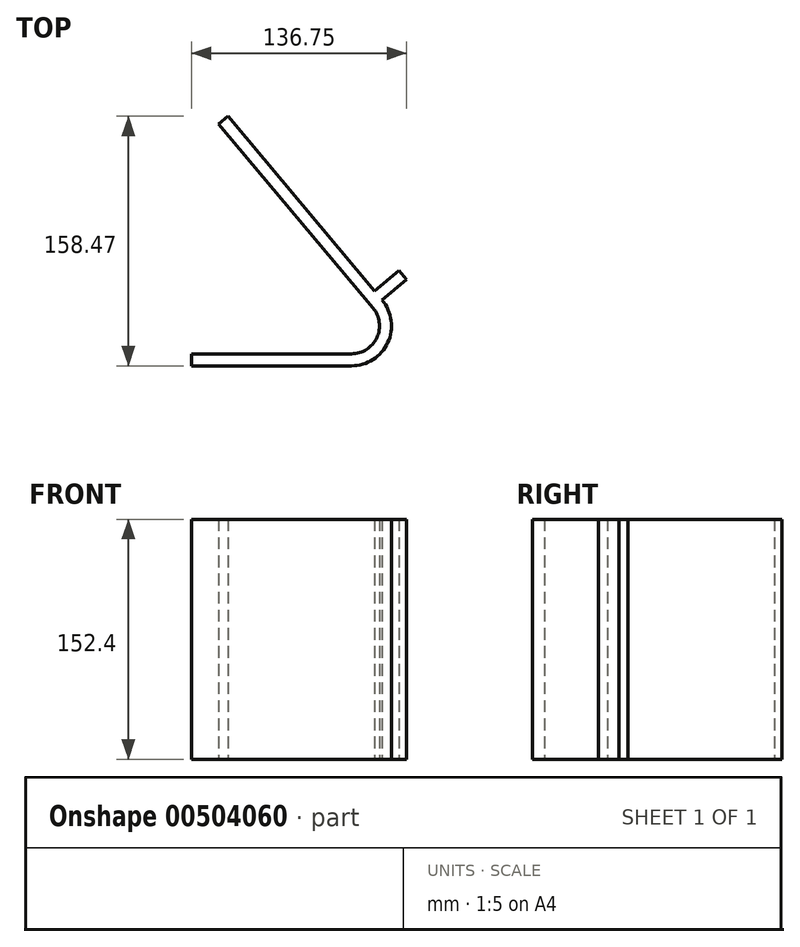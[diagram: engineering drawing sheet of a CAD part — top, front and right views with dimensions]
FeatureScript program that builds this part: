
annotation { "Feature Type Name" : "Feature", "Feature Type Description" : "" }
export const myFeature = defineFeature(function(context is Context, id is Id, definition is map)
    precondition{}
    {
        {
            var Q0;
            Q0=qCreatedBy(makeId("Top.planeOp"),FACE);
            var sketch = newSketch(context, id + "F0", { "sketchPlane" : qUnion([Q0])});
            skLineSegment(sketch, "E0", {"start": v(-114.2, -40.5) * mm, "end": v(-12.6, -40.5) * mm});
            skLineSegment(sketch, "E1", {"start": v(1.96, 7.06) * mm, "end": v(-91.1, 117.97) * mm});
            skPoint(sketch, "E2.visualSharp", {"position": v(41.87, -40.5) * mm});
            skArc(sketch, "E2.filletArc", {"start": v(-12.6, -40.5) * mm, "mid": v(10.42, -25.84) * mm, "end": v(6.86, 1.23) * mm});
            skLineSegment(sketch, "E3", {"start": v(-91.1, 117.97) * mm, "end": v(-96.94, 113.07) * mm});
            skLineSegment(sketch, "E4", {"start": v(-96.94, 113.07) * mm, "end": v(1.02, -3.67) * mm});
            skLineSegment(sketch, "E5", {"start": v(-12.6, -32.88) * mm, "end": v(-114.32, -32.88) * mm});
            skLineSegment(sketch, "E6", {"start": v(-114.32, -32.88) * mm, "end": v(-114.2, -40.5) * mm});
            skPoint(sketch, "E7.visualSharp", {"position": v(25.53, -32.88) * mm});
            skArc(sketch, "E7.filletArc", {"start": v(-12.6, -32.88) * mm, "mid": v(3.52, -22.62) * mm, "end": v(1.02, -3.67) * mm});
            skLineSegment(sketch, "E8", {"start": v(6.86, 1.23) * mm, "end": v(22.43, 14.29) * mm});
            skLineSegment(sketch, "E9", {"start": v(22.43, 14.29) * mm, "end": v(17.53, 20.12) * mm});
            skLineSegment(sketch, "E10", {"start": v(17.53, 20.12) * mm, "end": v(1.96, 7.06) * mm});
            skSolve(sketch);
        }
        {
            var Q0;
            Q0 = qSketchRegion(id + "F0", true);
            extrude(context, id + "F1", {"entities" : qUnion([Q0]), "depth" : 152.4 * mm});
        }
    });
